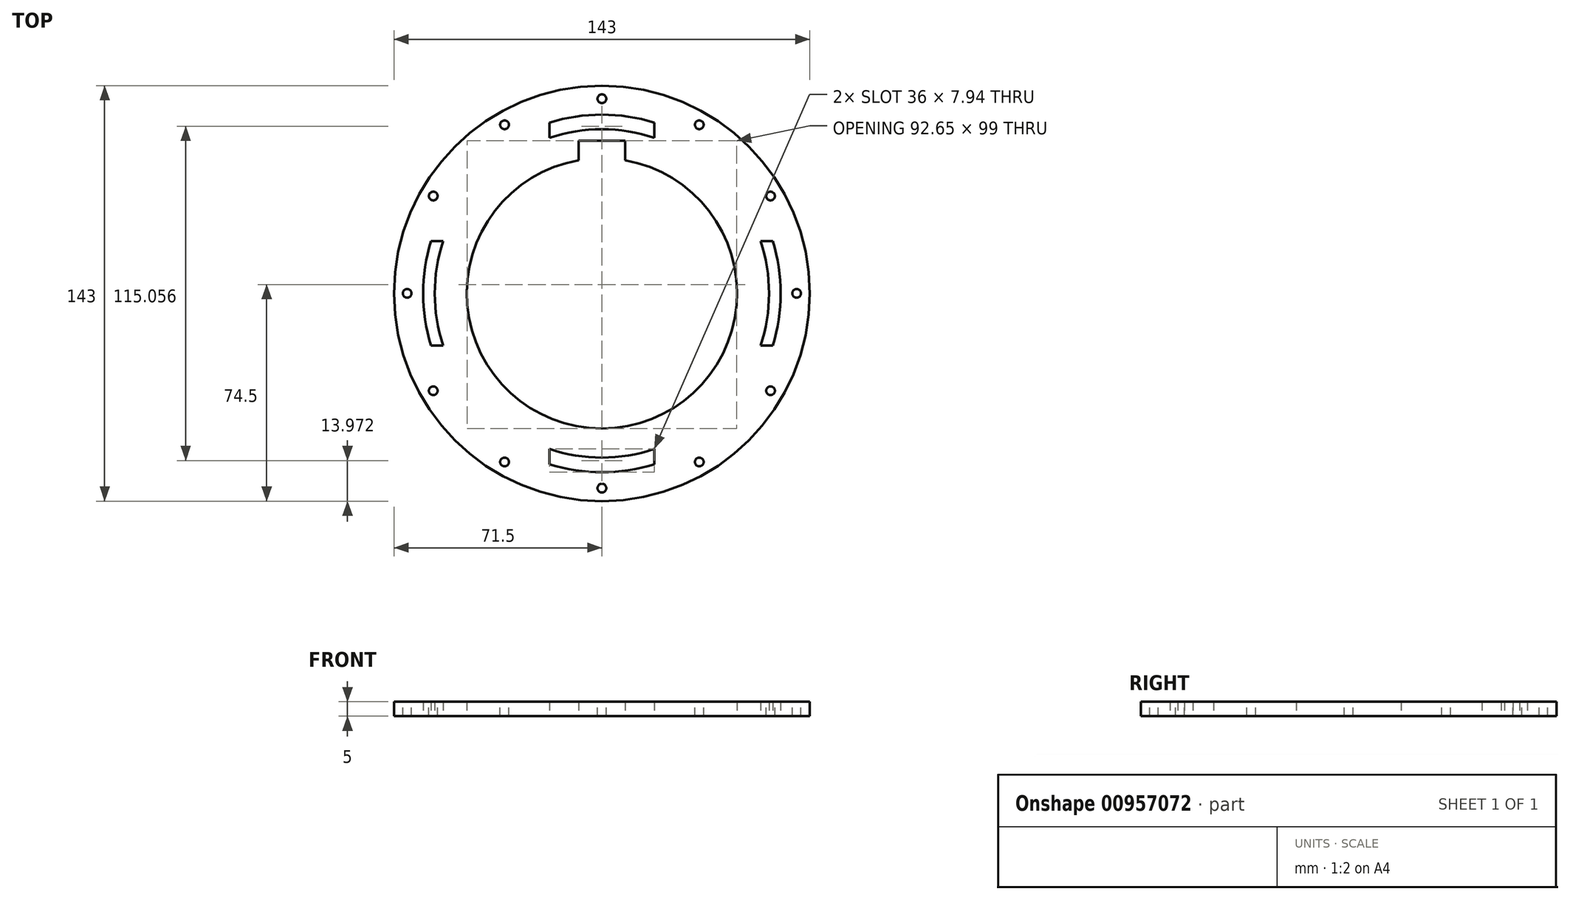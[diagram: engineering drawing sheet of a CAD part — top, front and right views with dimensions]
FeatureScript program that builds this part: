
annotation { "Feature Type Name" : "Feature", "Feature Type Description" : "" }
export const myFeature = defineFeature(function(context is Context, id is Id, definition is map)
    precondition{}
    {
        {
            var Q0;
            Q0=qCreatedBy(makeId("Top.planeOp"),FACE);
            var sketch = newSketch(context, id + "F0", { "sketchPlane" : qUnion([Q0])});
            skCircle(sketch, "E0", {"center": v(0, 0) * mm, "radius": 71.5 * mm});
            skArc(sketch, "E1", {"start": v(-42.87, -18) * mm, "mid": v(-32.88, -32.88) * mm, "end": v(-18, -42.87) * mm});
            skLineSegment(sketch, "E2.bottom", {"start": v(58.8, -18) * mm, "end": v(54.6, -18) * mm});
            skLineSegment(sketch, "E2.top", {"start": v(58.8, 18) * mm, "end": v(54.6, 18) * mm});
            skArc(sketch, "E3", {"start": v(58.8, -18) * mm, "mid": v(61.5, 0) * mm, "end": v(58.8, 18) * mm});
            skPoint(sketch, "E2.left.end.orphan", {"position": v(62.5, 18) * mm});
            skPoint(sketch, "E4.orphan", {"position": v(62.5, -18) * mm});
            skPoint(sketch, "E5.orphan", {"position": v(-62.5, 18) * mm});
            skPoint(sketch, "E6.orphan", {"position": v(-62.5, -18) * mm});
            skArc(sketch, "E7.trimOffspring", {"start": v(42.87, 18) * mm, "mid": v(32.88, 32.88) * mm, "end": v(18, 42.87) * mm});
            skLineSegment(sketch, "E8.trimOffspring", {"start": v(-54.6, 18) * mm, "end": v(-58.8, 18) * mm});
            skLineSegment(sketch, "E9.trimOffspring", {"start": v(-54.6, -18) * mm, "end": v(-58.8, -18) * mm});
            skLineSegment(sketch, "E10.left", {"start": v(18, -58.8) * mm, "end": v(18, -54.6) * mm});
            skLineSegment(sketch, "E10.right", {"start": v(-18, -58.8) * mm, "end": v(-18, -54.6) * mm});
            skPoint(sketch, "E11.orphan", {"position": v(-18, 62.5) * mm});
            skPoint(sketch, "E12.orphan", {"position": v(18, 62.5) * mm});
            skPoint(sketch, "E13.orphan", {"position": v(18, -62.5) * mm});
            skPoint(sketch, "E14.orphan", {"position": v(-18, -62.5) * mm});
            skLineSegment(sketch, "E15.trimOffspring", {"start": v(-18, 54.6) * mm, "end": v(-18, 58.8) * mm});
            skLineSegment(sketch, "E16.trimOffspring", {"start": v(18, 54.6) * mm, "end": v(18, 58.8) * mm});
            skArc(sketch, "E17.trimOffspring", {"start": v(-18, 42.87) * mm, "mid": v(-32.88, 32.88) * mm, "end": v(-42.87, 18) * mm});
            skArc(sketch, "E18.trimOffspring", {"start": v(18, -42.87) * mm, "mid": v(32.88, -32.88) * mm, "end": v(42.87, -18) * mm});
            skArc(sketch, "E19", {"start": v(54.6, -18) * mm, "mid": v(57.5, 0) * mm, "end": v(54.6, 18) * mm});
            skArc(sketch, "E20", {"start": v(-8, 45.8) * mm, "mid": v(0, -46.5) * mm, "end": v(8, 45.8) * mm});
            skArc(sketch, "E21.trimOffspring", {"start": v(-18, -58.8) * mm, "mid": v(0, -61.5) * mm, "end": v(18, -58.8) * mm});
            skArc(sketch, "E22.trimOffspring", {"start": v(-54.6, 18) * mm, "mid": v(-57.5, 0) * mm, "end": v(-54.6, -18) * mm});
            skArc(sketch, "E23.trimOffspring", {"start": v(-58.8, 18) * mm, "mid": v(-61.5, 0) * mm, "end": v(-58.8, -18) * mm});
            skArc(sketch, "E24.trimOffspring", {"start": v(18, 58.8) * mm, "mid": v(0, 61.5) * mm, "end": v(-18, 58.8) * mm});
            skLineSegment(sketch, "E25.top", {"start": v(8, 52.5) * mm, "end": v(-8, 52.5) * mm});
            skLineSegment(sketch, "E25.left", {"start": v(8, 45.8) * mm, "end": v(8, 52.5) * mm});
            skLineSegment(sketch, "E25.right", {"start": v(-8, 45.8) * mm, "end": v(-8, 52.5) * mm});
            skPoint(sketch, "E25.middle", {"position": v(0, 46.5) * mm});
            skPoint(sketch, "E26.orphan", {"position": v(-8, 40.5) * mm});
            skPoint(sketch, "E27.orphan", {"position": v(8, 40.5) * mm});
            skArc(sketch, "E28", {"start": v(-18, -53.56) * mm, "mid": v(0, -56.5) * mm, "end": v(18, -53.56) * mm});
            skLineSegment(sketch, "E29.left", {"start": v(-18, 54.6) * mm, "end": v(-18, 53.56) * mm});
            skLineSegment(sketch, "E29.right", {"start": v(18, 54.6) * mm, "end": v(18, 53.56) * mm});
            skLineSegment(sketch, "E30.left", {"start": v(-18, -54.6) * mm, "end": v(-18, -53.56) * mm});
            skLineSegment(sketch, "E30.right", {"start": v(18, -54.6) * mm, "end": v(18, -53.56) * mm});
            skArc(sketch, "E31.trimOffspring", {"start": v(18, 53.56) * mm, "mid": v(0, 56.5) * mm, "end": v(-18, 53.56) * mm});
            skSolve(sketch);
        }
        {
            var Q0;
            Q0 = qSketchRegion(id + "F0", true);
            extrude(context, id + "F1", {"entities" : qUnion([Q0]), "depth" : 5 * mm, "offsetDistance" : 25 * mm});
        }
        {
            var Q0;
            Q0=makeQuery(id+"F1.opExtrude","CAP_FACE",FACE,{"disambiguationData":[OSD([sQuery(id+"F0.wireOp",EDGE,"E0"),sQuery(id+"F0.wireOp",EDGE,"E2.bottom"),sQuery(id+"F0.wireOp",EDGE,"E2.top"),sQuery(id+"F0.wireOp",EDGE,"E3"),sQuery(id+"F0.wireOp",EDGE,"E8.trimOffspring"),sQuery(id+"F0.wireOp",EDGE,"E9.trimOffspring"),sQuery(id+"F0.wireOp",EDGE,"E10.left"),sQuery(id+"F0.wireOp",EDGE,"E10.right"),sQuery(id+"F0.wireOp",EDGE,"E15.trimOffspring"),sQuery(id+"F0.wireOp",EDGE,"E16.trimOffspring"),sQuery(id+"F0.wireOp",EDGE,"E19"),sQuery(id+"F0.wireOp",EDGE,"E20"),sQuery(id+"F0.wireOp",EDGE,"E21.trimOffspring"),sQuery(id+"F0.wireOp",EDGE,"a3b893ac-4a70-4967-a853-bd6a71a1c1f9.trimOffspring"),sQuery(id+"F0.wireOp",EDGE,"E22.trimOffspring"),sQuery(id+"F0.wireOp",EDGE,"E23.trimOffspring"),sQuery(id+"F0.wireOp",EDGE,"b58ed8b9-2146-478b-a0e9-ccbe54b94f8e.trimOffspring"),sQuery(id+"F0.wireOp",EDGE,"E24.trimOffspring"),sQuery(id+"F0.wireOp",EDGE,"E25.top"),sQuery(id+"F0.wireOp",EDGE,"E25.left"),sQuery(id+"F0.wireOp",EDGE,"E25.right")])],"isStart":false});
            var sketch = newSketch(context, id + "F2", { "sketchPlane" : qUnion([Q0])});
            skCircle(sketch, "E32", {"center": v(0, 0) * mm, "radius": 67 * mm, "construction": true});
            skCircle(sketch, "E33", {"center": v(67, 0) * mm, "radius": 1.5 * mm});
            skPoint(sketch, "E33.centerSnap0", {"position": v(57.5, 0) * mm});
            skCircle(sketch, "E34.1.0", {"center": v(58.02, 33.5) * mm, "radius": 1.5 * mm});
            skCircle(sketch, "E34.2.0", {"center": v(33.5, 58.02) * mm, "radius": 1.5 * mm});
            skCircle(sketch, "E34.3.0", {"center": v(0, 67) * mm, "radius": 1.5 * mm});
            skCircle(sketch, "E34.4.0", {"center": v(-33.5, 58.02) * mm, "radius": 1.5 * mm});
            skCircle(sketch, "E34.5.0", {"center": v(-58.02, 33.5) * mm, "radius": 1.5 * mm});
            skCircle(sketch, "E34.6.0", {"center": v(-67, 0) * mm, "radius": 1.5 * mm});
            skCircle(sketch, "E34.7.0", {"center": v(-58.02, -33.5) * mm, "radius": 1.5 * mm});
            skCircle(sketch, "E34.8.0", {"center": v(-33.5, -58.02) * mm, "radius": 1.5 * mm});
            skCircle(sketch, "E34.9.0", {"center": v(0, -67) * mm, "radius": 1.5 * mm});
            skCircle(sketch, "E34.10.0", {"center": v(33.5, -58.02) * mm, "radius": 1.5 * mm});
            skCircle(sketch, "E34.11.0", {"center": v(58.02, -33.5) * mm, "radius": 1.5 * mm});
            skSolve(sketch);
        }
        {
            var Q0;
            Q0 = qSketchRegion(id + "F2", true);
            extrude(context, id + "F3", {"entities" : qUnion([Q0]), "operationType" : NewBodyOperationType.REMOVE, "endBound" : BoundingType.THROUGH_ALL, "oppositeDirection" : true, "depth" : 25 * mm, "offsetDistance" : 25 * mm});
        }
    });
